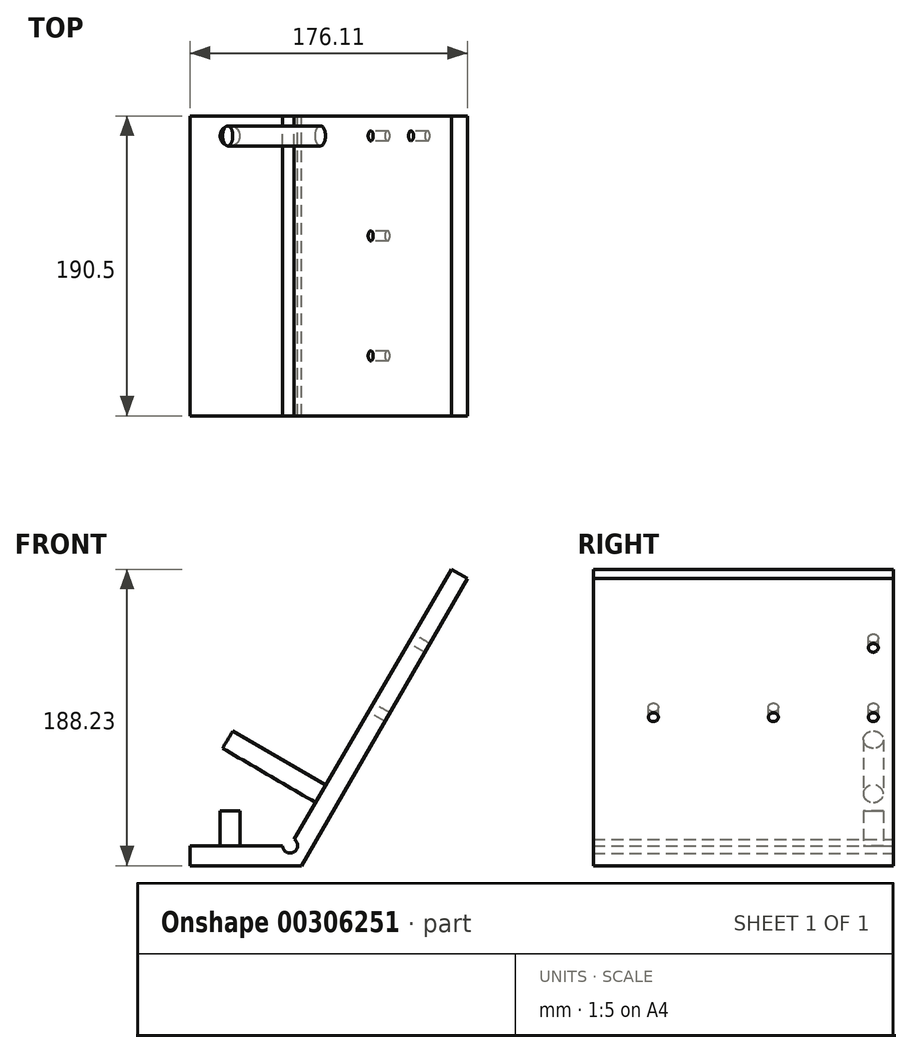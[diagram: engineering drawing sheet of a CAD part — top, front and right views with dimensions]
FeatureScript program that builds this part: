
annotation { "Feature Type Name" : "Feature", "Feature Type Description" : "" }
export const myFeature = defineFeature(function(context is Context, id is Id, definition is map)
    precondition{}
    {
        {
            var Q0;
            Q0=qCreatedBy(makeId("Front.planeOp"),FACE);
            var sketch = newSketch(context, id + "F0", { "sketchPlane" : qUnion([Q0])});
            skLineSegment(sketch, "E0", {"start": v(0, 0) * mm, "end": v(70.84, 0) * mm});
            skLineSegment(sketch, "E1.0", {"start": v(0, 12.7) * mm, "end": v(58.74, 12.7) * mm});
            skLineSegment(sketch, "E2", {"start": v(0, 0) * mm, "end": v(0, 12.7) * mm});
            skArc(sketch, "E3", {"start": v(58.74, 12.7) * mm, "mid": v(65.87, 8.57) * mm, "end": v(65.9, 16.81) * mm});
            skLineSegment(sketch, "E4", {"start": v(70.84, 0) * mm, "end": v(176.11, 182.33) * mm});
            skLineSegment(sketch, "E5", {"start": v(176.11, 182.33) * mm, "end": v(165.9, 188.23) * mm});
            skLineSegment(sketch, "E6", {"start": v(165.9, 188.23) * mm, "end": v(65.9, 16.81) * mm});
            skSolve(sketch);
        }
        {
            var Q0;
            Q0 = qSketchRegion(id + "F0", true);
            extrude(context, id + "F1", {"entities" : qUnion([Q0]), "depth" : 190.5 * mm});
        }
        {
            var Q0;
            Q0=makeQuery(id+"F1.opExtrude","SWEPT_FACE",FACE,{"disambiguationData":[OSD([sQuery(id+"F0.wireOp",EDGE,"E1.0")])]});
            var sketch = newSketch(context, id + "F2", { "sketchPlane" : qUnion([Q0])});
            skLineSegment(sketch, "E7", {"start": v(0, 0) * mm, "end": v(25.4, 0) * mm});
            skLineSegment(sketch, "E8", {"start": v(25.4, 0) * mm, "end": v(25.4, -12.7) * mm});
            skCircle(sketch, "E9", {"center": v(25.4, -12.7) * mm, "radius": 6.35 * mm});
            skSolve(sketch);
        }
        {
            var Q0;
            Q0 = qSketchRegion(id + "F2", true);
            extrude(context, id + "F3", {"entities" : qUnion([Q0]), "operationType" : NewBodyOperationType.ADD, "depth" : 22 * mm});
        }
        {
            var Q0;
            Q0=makeQuery(id+"F1.opExtrude","SWEPT_FACE",FACE,{"disambiguationData":[OSD([sQuery(id+"F0.wireOp",EDGE,"E6")])]});
            var sketch = newSketch(context, id + "F4", { "sketchPlane" : qUnion([Q0])});
            skCircle(sketch, "E10", {"center": v(12.7, 195.38) * mm, "radius": 3.17 * mm});
            skCircle(sketch, "E11", {"center": v(12.7, 144.58) * mm, "radius": 3.18 * mm});
            skCircle(sketch, "E12", {"center": v(76.2, 144.58) * mm, "radius": 3.18 * mm});
            skCircle(sketch, "E13", {"center": v(152.4, 144.58) * mm, "radius": 3.18 * mm});
            skCircle(sketch, "E14", {"center": v(12.7, 81.13) * mm, "radius": 6.35 * mm});
            skSolve(sketch);
        }
        {
            var Q0;
            Q0=makeQuery(id+"F4.imprint","IMPRINT",FACE,{"disambiguationData":[TD([[makeQuery(id+"F4.imprint","IMPRINT",EDGE,{"derivedFrom":sQuery(id+"F4.wireOp",EDGE,"E14")}),1.0]])]});
            extrude(context, id + "F5", {"entities" : qUnion([Q0]), "operationType" : NewBodyOperationType.ADD, "depth" : 68.15 * mm});
        }
        {
            var Q0;
            Q0=sQuery(id+"F4.wireOp",VERTEX,"E10.center");
            var Q1;
            Q1=sQuery(id+"F4.wireOp",VERTEX,"E11.center");
            var Q2;
            Q2=sQuery(id+"F4.wireOp",VERTEX,"E12.center");
            var Q3;
            Q3=sQuery(id+"F4.wireOp",VERTEX,"E13.center");
            var Q4;
            Q4=makeQuery(id+"F1.opExtrude","SWEPT_BODY",BODY,{"disambiguationData":[OSD([sQuery(id+"F0.wireOp",EDGE,"E0"),sQuery(id+"F0.wireOp",EDGE,"E1.0"),sQuery(id+"F0.wireOp",EDGE,"E2"),sQuery(id+"F0.wireOp",EDGE,"E3"),sQuery(id+"F0.wireOp",EDGE,"E4"),sQuery(id+"F0.wireOp",EDGE,"E5"),sQuery(id+"F0.wireOp",EDGE,"E6")])]});
            hole(context, id + "F6", {"style" : HoleStyle.SIMPLE, "endStyle" : HoleEndStyle.THROUGH, "holeDiameter" : 6.35 * mm, "tappedDepth" : 12.7 * mm, "tapClearance" : 3, "locations" : qUnion([Q0, Q1, Q2, Q3]), "scope" : qUnion([Q4])});
        }
    });
